FCSTD DOCUMENT  (FreeCAD 1.0RUnknown)
Label: mastersketch
License: All rights reserved
LicenseURL: https://en.wikipedia.org/wiki/All_rights_reserved
objects: Sketcher::SketchObject×2, PartDesign::Body×1, Spreadsheet::Sheet×1
note: 5 computed .brp shape members not serialized (recipe doc carries the construction recipe); baked Part::Feature solids carry a one-line shape summary decoded from their .brp

FEATURE [Sketcher::SketchObject] Sketch  label="doors"
  ArcFitTolerance = 1e-06
  AttachmentSupport = -> [XZ_Plane]
  FullyConstrained = true
  MakeInternals = false
  MapMode = 5
  Placement = pos=(0,0,0) rot=(1,0,0;1.5708rad)
  expr: Constraints[23] = Spreadsheet.corpus_width - 5
  expr: Constraints[33] = Spreadsheet.hettich_height
  expr: Constraints[46] = Spreadsheet.corpus_width - 5
  expr: Constraints[58] = Spreadsheet.corpus_width - 5
  sketch-geometry (29):
    g0: LineSegment StartX=0 StartY=0 StartZ=0 EndX=0 EndY=2480 EndZ=0
    g1: LineSegment StartX=0 StartY=2480 StartZ=0 EndX=-220 EndY=2480 EndZ=0
    g2: LineSegment StartX=0 StartY=0 StartZ=0 EndX=-2160 EndY=0 EndZ=0
    g3: LineSegment StartX=-2160 StartY=0 StartZ=0 EndX=-2160 EndY=210 EndZ=0
    g4: LineSegment StartX=-2160 StartY=210 StartZ=0 EndX=-220 EndY=2480 EndZ=0
    g5: LineSegment StartX=-12.5 StartY=30 StartZ=0 EndX=-12.5 EndY=2081.4 EndZ=0
    g6: LineSegment StartX=-12.5 StartY=2081.4 StartZ=0 EndX=-547.5 EndY=2081.4 EndZ=0
    g7: LineSegment StartX=-547.5 StartY=2081.4 StartZ=0 EndX=-547.5 EndY=30 EndZ=0
    g8: LineSegment StartX=-547.5 StartY=30 StartZ=0 EndX=-12.5 EndY=30 EndZ=0
    g9: LineSegment StartX=-2160 StartY=194.608 StartZ=0 EndX=-206.846 EndY=2480 EndZ=0
    g10: LineSegment StartX=-2160 StartY=30 StartZ=0 EndX=0 EndY=30 EndZ=0
    g11: LineSegment StartX=-552.5 StartY=30 StartZ=0 EndX=-552.5 EndY=1449.54 EndZ=0
    g12: LineSegment StartX=-552.5 StartY=1449.54 StartZ=0 EndX=-1087.5 EndY=1449.54 EndZ=0
    g13: LineSegment StartX=-1087.5 StartY=1449.54 StartZ=0 EndX=-1087.5 EndY=30 EndZ=0
    g14: LineSegment StartX=-1087.5 StartY=30 StartZ=0 EndX=-552.5 EndY=30 EndZ=0
    g15: LineSegment StartX=-1627.5 StartY=30 StartZ=0 EndX=-1092.5 EndY=30 EndZ=0
    g16: LineSegment StartX=-1092.5 StartY=30 StartZ=0 EndX=-1092.5 EndY=817.688 EndZ=0
    g17: LineSegment StartX=-1092.5 StartY=817.688 StartZ=0 EndX=-1627.5 EndY=817.688 EndZ=0
    g18: LineSegment StartX=-1627.5 StartY=817.688 StartZ=0 EndX=-1627.5 EndY=30 EndZ=0
    g19: LineSegment StartX=-1632.5 StartY=811.837 StartZ=0 EndX=-1632.5 EndY=30 EndZ=0
    g20: LineSegment StartX=-12.5 StartY=2081.4 StartZ=0 EndX=-12.5 EndY=2470 EndZ=0
    g21: LineSegment StartX=-552.5 StartY=1449.54 StartZ=0 EndX=-552.5 EndY=2075.55 EndZ=0
    g22: LineSegment StartX=-1092.5 StartY=817.688 StartZ=0 EndX=-1092.5 EndY=1443.69 EndZ=0
    g23: LineSegment [constr] StartX=-12.5 StartY=2470 StartZ=0 EndX=-215.392 EndY=2470 EndZ=0
    g24: LineSegment [constr] StartX=-2147.5 StartY=209.234 StartZ=0 EndX=-2147.5 EndY=30 EndZ=0
    g25: LineSegment [constr] StartX=-2150 StartY=177.064 StartZ=0 EndX=-1627.5 EndY=788.443 EndZ=0
    g26: LineSegment [constr] StartX=-1904.57 StartY=493.489 StartZ=0 EndX=-1890.12 EndY=481.145 EndZ=0
    g27: LineSegment [constr] StartX=-2147.5 StartY=49 StartZ=0 EndX=-1627.5 EndY=49 EndZ=0
    g28: LineSegment [constr] StartX=-2150 StartY=177.064 StartZ=0 EndX=-2150 EndY=49 EndZ=0
  constraints (107):
    c: Distance(g0) = 2480
    c: Coincident(g0,g-1)
    c: PointOnObject(g0,g-2)
    c: Distance(g1) = 220
    c: Coincident(g1,g0)
    c: Horizontal(g1)
    c: Distance(g2) = 2160
    c: Coincident(g2,g0)
    c: PointOnObject(g2,g-1)
    c: Distance(g3) = 210
    c: Coincident(g3,g2)
    c: Vertical(g3)
    c: Coincident(g4,g3)
    c: Coincident(g4,g1)
    c: Coincident(g5,g6)
    c: Coincident(g6,g7)
    c: Coincident(g7,g8)
    c: Coincident(g8,g5)
    c: Vertical(g5)
    c: Vertical(g7)
    c: Horizontal(g6)
    c: Horizontal(g8)
    c: Distance(g0,g5) = 12.5
    c: DistanceX(g6,g6) = 535
    c: DistanceY(g5,g5) = 2051.4  'corpus00_height'
    c: PointOnObject(g9,g3)
    c: PointOnObject(g9,g1)
    c: Parallel(g4,g9)
    c: Distance(g3,g9) = 10
    c: PointOnObject(g6,g9)
    c: PointOnObject(g10,g3)
    c: PointOnObject(g10,g0)
    c: Horizontal(g10)
    c: Distance(g2,g10) = 30
    c: PointOnObject(g7,g10)
    c: Coincident(g11,g12)
    c: Coincident(g12,g13)
    c: Coincident(g13,g14)
    c: Coincident(g14,g11)
    c: Vertical(g11)
    c: Vertical(g13)
    c: Horizontal(g12)
    c: Horizontal(g14)
    c: PointOnObject(g11,g10)
    c: PointOnObject(g12,g9)
    c: Distance(g7,g11) = 5
    c: DistanceX(g12,g12) = 535
    c: Distance(g10,g12) = 1419.54  'corpus01_height'
    c: Coincident(g15,g16)
    c: Coincident(g16,g17)
    c: Coincident(g17,g18)
    c: Coincident(g18,g15)
    c: Horizontal(g15)
    c: Horizontal(g17)
    c: Vertical(g16)
    c: Vertical(g18)
    c: PointOnObject(g15,g10)
    c: PointOnObject(g17,g9)
    c: Distance(g16,g18) = 535
    c: Distance(g10,g17) = 787.688  'corpus02_height'
    c: Distance(g13,g16) = 5
    c: PointOnObject(g19,g9)
    c: PointOnObject(g19,g10)
    c: Vertical(g19)
    c: Distance(g18,g19) = 5
    c: DistanceY(g19,g19) = 781.837  'corpus03_door_height'
    c: Coincident(g20,g5)
    c: Vertical(g20)
    c: Distance(g20,g1) = 10
    c: Distance(g20,g8) = 2440  'corpus00_door_height'
    c: Coincident(g21,g11)
    c: Vertical(g21)
    c: Distance(g21,g10) = 2045.55  'corpus01_door_height'
    c: Coincident(g22,g16)
    c: Vertical(g22)
    c: PointOnObject(g21,g9)
    c: PointOnObject(g22,g9)
    c: Distance(g22,g10) = 1413.69  'corpus02_door_height'
    c: Angle(g3,g4) = 2.43442  'alpha'
    c: Distance(g6,g8) = 2051.4
    c: Coincident(g23,g20)
    c: PointOnObject(g23,g9)
    c: Horizontal(g23)
    c: DistanceX(g23,g23) = 202.892  'corpus00_door_top'
    c: PointOnObject(g24,g10)
    c: Vertical(g24)
    c: Distance(g3,g24) = 12.5
    c: Distance(g19,g24) = 515  'corpus03_door_width'
    c: PointOnObject(g25,g18)
    c: Parallel(g25,g9)
    c: PointOnObject(g26,g9)
    c: PointOnObject(g26,g25)
    c: Perpendicular(g25,g26)
    c: Distance(g26,g25) = 400
    c: Distance(g26,g26) = 19
    c: Distance(g25,g25) = 804.233  'corpus03_top'
    c: PointOnObject(g27,g24)
    c: PointOnObject(g27,g18)
    c: Horizontal(g27)
    c: Distance(g10,g27) = 19
    c: DistanceY(g27,g25) = 739.443  'corpus03_right_height'
    c: Vertical(g28)
    c: Horizontal(g28,g27)
    c: Distance(g28,g3) = 10
    c: DistanceY(g28,g28) = 128.064  'corpus03_left_height'
    c: Coincident(g28,g25)
    c: PointOnObject(g24,g9)
FEATURE [Sketcher::SketchObject] Sketch001  label="corpus"
  ArcFitTolerance = 1e-06
  AttachmentOffset = pos=(0,0,-20) rot=(0,0,1;0rad)
  AttachmentSupport = -> [XZ_Plane]
  ExternalGeometry = -> [Sketch]
  FullyConstrained = true
  MakeInternals = false
  MapMode = 5
  Placement = pos=(0,20,-4.4e-15) rot=(1,0,0;1.5708rad)
  expr: Constraints[22] = .Constraints.corpus_width
  expr: Constraints[33] = .Constraints.corpus_width
  expr: Constraints[55] = <<doors>>.Constraints.alpha
  expr: Constraints[65] = <<doors>>.Constraints.alpha
  sketch-geometry (29):
    g0: LineSegment StartX=-550 StartY=2078.47 StartZ=0 EndX=-550 EndY=30 EndZ=0
    g1: LineSegment StartX=-550 StartY=30 StartZ=0 EndX=-10 EndY=30 EndZ=0
    g2: LineSegment StartX=-10 StartY=30 StartZ=0 EndX=-10 EndY=2078.47 EndZ=0
    g3: LineSegment StartX=-10 StartY=2078.47 StartZ=0 EndX=-550 EndY=2078.47 EndZ=0
    g4: LineSegment StartX=-550 StartY=30 StartZ=0 EndX=-550 EndY=1446.62 EndZ=0
    g5: LineSegment StartX=-550 StartY=1446.62 StartZ=0 EndX=-1090 EndY=1446.62 EndZ=0
    g6: LineSegment StartX=-1090 StartY=1446.62 StartZ=0 EndX=-1090 EndY=30 EndZ=0
    g7: LineSegment StartX=-1090 StartY=30 StartZ=0 EndX=-550 EndY=30 EndZ=0
    g8: LineSegment StartX=-1090 StartY=30 StartZ=0 EndX=-1090 EndY=814.763 EndZ=0
    g9: LineSegment StartX=-1090 StartY=814.763 StartZ=0 EndX=-1630 EndY=814.763 EndZ=0
    g10: LineSegment StartX=-1630 StartY=814.763 StartZ=0 EndX=-1630 EndY=30 EndZ=0
    g11: LineSegment StartX=-1630 StartY=30 StartZ=0 EndX=-1090 EndY=30 EndZ=0
    g12: LineSegment StartX=-2150 StartY=30 StartZ=0 EndX=-1630 EndY=30 EndZ=0
    g13: LineSegment StartX=-1630 StartY=30 StartZ=0 EndX=-1630 EndY=49 EndZ=0
    g14: LineSegment StartX=-1630 StartY=49 StartZ=0 EndX=-2150 EndY=49 EndZ=0
    g15: LineSegment StartX=-2150 StartY=49 StartZ=0 EndX=-2150 EndY=30 EndZ=0
    g16: LineSegment StartX=-1649 StartY=49 StartZ=0 EndX=-1630 EndY=49 EndZ=0
    g17: LineSegment StartX=-1630 StartY=49 StartZ=0 EndX=-1630 EndY=785.518 EndZ=0
    g18: LineSegment StartX=-1649 StartY=763.286 StartZ=0 EndX=-1649 EndY=49 EndZ=0
    g19: LineSegment StartX=-1630 StartY=785.518 StartZ=0 EndX=-1649 EndY=763.286 EndZ=0
    g20: LineSegment StartX=-2150 StartY=49 StartZ=0 EndX=-2131 EndY=49 EndZ=0
    g21: LineSegment StartX=-2131 StartY=49 StartZ=0 EndX=-2131 EndY=199.296 EndZ=0
    g22: LineSegment StartX=-2150 StartY=177.064 StartZ=0 EndX=-2150 EndY=49 EndZ=0
    g23: LineSegment StartX=-2131 StartY=199.296 StartZ=0 EndX=-2150 EndY=177.064 EndZ=0
    g24: LineSegment StartX=-2150 StartY=177.064 StartZ=0 EndX=-2150 EndY=206.309 EndZ=0
    g25: LineSegment StartX=-2150 StartY=206.309 StartZ=0 EndX=-1630 EndY=814.763 EndZ=0
    g26: LineSegment StartX=-1630 StartY=814.763 StartZ=0 EndX=-1630 EndY=785.518 EndZ=0
    g27: LineSegment StartX=-1630 StartY=785.518 StartZ=0 EndX=-2150 EndY=177.064 EndZ=0
    g28: LineSegment [constr] StartX=-2150 StartY=206.309 StartZ=0 EndX=-2135.56 EndY=193.965 EndZ=0
  constraints (86):
    c: Coincident(g0,g1)
    c: Coincident(g1,g2)
    c: Coincident(g2,g3)
    c: Coincident(g3,g0)
    c: Vertical(g0)
    c: Vertical(g2)
    c: Horizontal(g1)
    c: Horizontal(g3)
    c: PointOnObject(g1,g-8)
    c: Distance(g-5,g2) = 10
    c: Distance(g2,g0) = 540  'corpus_width'
    c: Coincident(g4,g5)
    c: Coincident(g5,g6)
    c: Coincident(g6,g7)
    c: Coincident(g7,g4)
    c: Vertical(g4)
    c: Vertical(g6)
    c: Horizontal(g5)
    c: Horizontal(g7)
    c: Coincident(g4,g0)
    c: PointOnObject(g0,g-9)
    c: PointOnObject(g5,g-9)
    c: DistanceX(g6,g0) = 540
    c: Coincident(g8,g9)
    c: Coincident(g9,g10)
    c: Coincident(g10,g11)
    c: Coincident(g11,g8)
    c: Vertical(g8)
    c: Vertical(g10)
    c: Horizontal(g9)
    c: Horizontal(g11)
    c: Coincident(g8,g6)
    c: PointOnObject(g9,g-9)
    c: DistanceX(g10,g6) = 540
    c: Coincident(g12,g13)
    c: Coincident(g13,g14)
    c: Coincident(g14,g15)
    c: Coincident(g15,g12)
    c: Horizontal(g12)
    c: Horizontal(g14)
    c: Vertical(g13)
    c: Vertical(g15)
    c: PointOnObject(g12,g-8)
    c: PointOnObject(g13,g10)
    c: Distance(g12,g14) = 19
    c: DistanceX(g-8,g12) = 10
    c: Coincident(g16,g17)
    c: Coincident(g18,g16)
    c: Horizontal(g16)
    c: Vertical(g17)
    c: Vertical(g18)
    c: PointOnObject(g16,g14)
    c: PointOnObject(g17,g10)
    c: Coincident(g19,g17)
    c: Coincident(g18,g19)
    c: Angle(g18,g19) = 2.43442
    c: Distance(g16,g13) = 19
    c: Coincident(g20,g21)
    c: Coincident(g22,g20)
    c: Horizontal(g20)
    c: Vertical(g21)
    c: Vertical(g22)
    c: Coincident(g20,g14)
    c: Coincident(g23,g21)
    c: Coincident(g22,g23)
    c: Angle(g22,g23) = 2.43442
    c: Distance(g14,g20) = 19
    c: Coincident(g24,g22)
    c: Vertical(g24)
    c: Coincident(g25,g24)
    c: PointOnObject(g25,g10)
    c: Coincident(g26,g25)
    c: Coincident(g26,g17)
    c: Coincident(g27,g17)
    c: Coincident(g27,g22)
    c: Parallel(g27,g25)
    c: Parallel(g25,g-9)
    c: Coincident(g28,g24)
    c: PointOnObject(g28,g23)
    c: Perpendicular(g27,g28)
    c: Distance(g28,g28) = 19
    c: PointOnObject(g25,g-9)
    c: DistanceY(g13,g17) = 736.518  'corpus03_right_height'
    c: DistanceY(g22,g22) = 128.064  'corpus03_left_height'
    c: DistanceY(g10,g9) = 784.763  'corpus03_back_height'
    c: DistanceX(g14,g10) = 520  'corpus03_width'
FEATURE [PartDesign::Body] Body
  AllowCompound = false
  Group = -> [Sketch,Sketch001]
  Origin = -> Origin
FEATURE [Spreadsheet::Sheet] Spreadsheet
  cells = A1='corpus_width; B1(corpus_width)=540; A2='corpus_depth; B2(corpus_depth)=600; A3='corpus_outer_thickness; B3(corpus_outer_thickness)=19; A4='corpus_backplate_thickness; B4(corpus_backplate_thickness)=19; A5='corpus_heigth; B5(corpus_height)=2045; A6='corpus01_heigth; B6(corpus01_height)=1415; A7='corpus02_heigth; B7(corpus02_height)=780; A8='drawer_outer_thickness; B8(drawer_outer_thickness)=19; A9='drawer_bottom_thickness; B9(drawer_bottom_thickness)=6; A10='drawer_length; B10(drawer_length)==B2 - 50; A11='drawer_width; B11(drawer_width)==B1 - 2 * 12.5 - 2 * B3; A12='drawer_bottom_tol; B12(drawer_bottom_tol)=0.5; A13='drawer_height; B13(drawer_height)=170; A14='drawer_slot_depth; B14(drawer_slot_depth)=8; A15='drawer_slot_height; B15(drawer_slot_height)=10; A16='hettich_height; B16(hettich_height)=30
